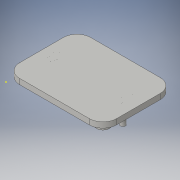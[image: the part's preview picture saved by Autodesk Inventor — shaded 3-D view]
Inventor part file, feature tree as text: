
AUTODESK INVENTOR PART (.ipt)
format: ipt  version: 2016 (Build 200138000, 138)  size: 180,736 bytes
history: native  units: in
note: dims shown in document units (in); Inventor stores cm internally (conversion verified against a paired STEP export)
features: sketch x6, extrude x5, fillet x1, projected_geometry x1
ambient origin geometry x8: Origin, YZ Plane, XZ Plane, XY Plane, X Axis, Y Axis, Z Axis, Center Point
bodies: Solid1 (feature_tree)
feature tree (13):
  extrude  "Extrusion1"  Depth=2.6in
  extrude  "Extrusion2"  Depth=0.2in
  extrude  "Extrusion3"  Depth=0.12in
  sketch  "Sketch4"  dims[d7=0.12in d8=0.12in d9=0.102in d10=0.0in]
  extrude  "Extrusion4"  Depth=0.102in
  fillet  "Fillet1"  Radius=0.102in
  extrude  "Extrusion5"  Depth=0.4in
  sketch  "Sketch1"  dims[d0=3.55in d1=2.6in]
  sketch  "Sketch2"  dims[d2=0.2in d3=0.0in d4=0.4625in]
  projected_geometry  "Projected Loop1"
  sketch  "Sketch3"  dims[d5=0.12in d6=0.12in]
  sketch  "Sketch5"  dims[d11=0.253in d12=0.4in]
  sketch  "Sketch6"  dims[d14=0.253in d15=0.63in d16=0.16in d17=0.0in d18=0.23in d19=0.325in d20=0.35in d21=0.0in d22=0.5in d23=0.18in d24=0.18in d25=0.75in d26=0.0in]
